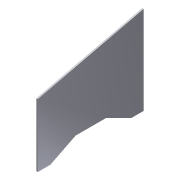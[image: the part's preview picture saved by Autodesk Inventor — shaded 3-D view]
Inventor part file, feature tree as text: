
AUTODESK INVENTOR PART (.ipt)
format: ipt  version: 2014 (Build 180170000, 170)  size: 92,672 bytes
history: native  units: mm
features: extrude x3, sketch x3
ambient origin geometry x8: Origin, YZ Plane, XZ Plane, XY Plane, X Axis, Y Axis, Z Axis, Center Point
bodies: Solid1 (feature_tree)
feature tree (6):
  extrude  "Extrusion1"  Depth=210.0mm
  extrude  "Extrusion2"  Depth=25.0mm
  extrude  "Extrusion3"  Depth=3.0mm TaperAngle=0.0deg
  sketch  "Sketch1"  dims[d0=150.0mm d1=210.0mm]
  sketch  "Sketch2"  dims[d2=3.0mm d3=0.0mm d4=25.0mm]
  sketch  "Sketch3"  dims[d5=50.0mm d6=3.0mm d7=0.0mm d8=50.0mm d9=3.0mm d10=0.0mm]
